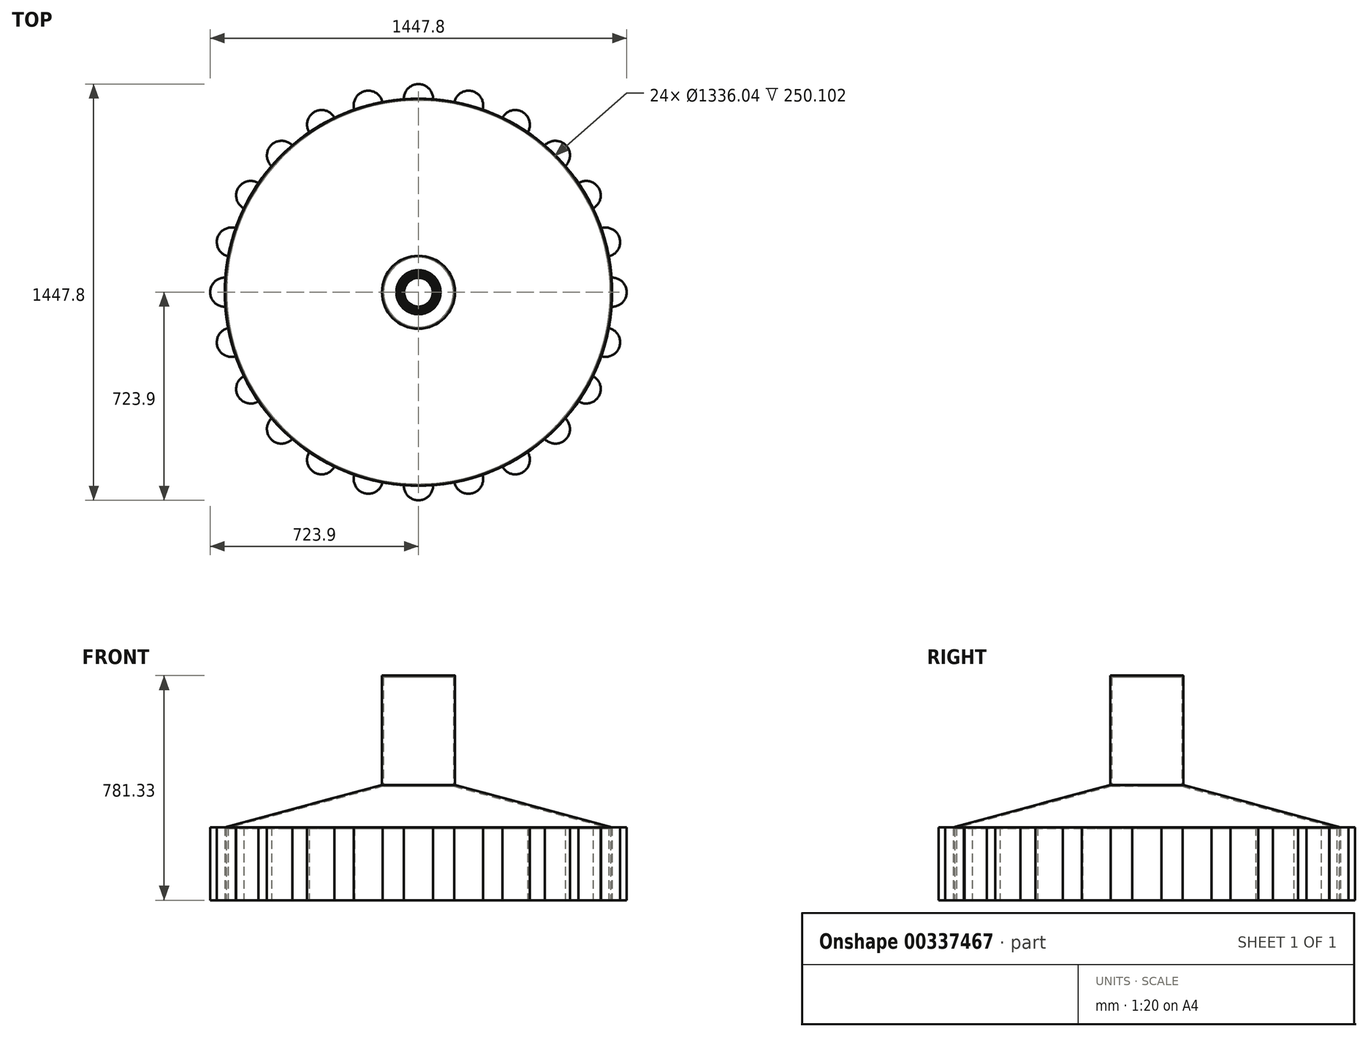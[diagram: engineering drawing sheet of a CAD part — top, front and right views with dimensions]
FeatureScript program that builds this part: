
annotation { "Feature Type Name" : "Feature", "Feature Type Description" : "" }
export const myFeature = defineFeature(function(context is Context, id is Id, definition is map)
    precondition{}
    {
        {
            var Q0;
            Q0=qCreatedBy(makeId("Front.planeOp"),FACE);
            var sketch = newSketch(context, id + "F0", { "sketchPlane" : qUnion([Q0])});
            skLineSegment(sketch, "E0", {"start": v(-673.1, 0) * mm, "end": v(-673.1, 254) * mm});
            skLineSegment(sketch, "E1", {"start": v(-673.1, 254) * mm, "end": v(-127, 400.33) * mm});
            skLineSegment(sketch, "E2", {"start": v(-127, 400.33) * mm, "end": v(-127, 781.33) * mm});
            skLineSegment(sketch, "E3", {"start": v(0, 0) * mm, "end": v(0, 880.24) * mm, "construction": true});
            skLineSegment(sketch, "E4", {"start": v(-127, 781.33) * mm, "end": v(0, 781.33) * mm});
            skLineSegment(sketch, "E5", {"start": v(0, 781.33) * mm, "end": v(0, 0) * mm});
            skLineSegment(sketch, "E6", {"start": v(-673.1, 0) * mm, "end": v(0, 0) * mm});
            skSolve(sketch);
        }
        {
            var Q0;
            Q0=makeQuery(id+"F0.imprint","IMPRINT",FACE,{"disambiguationData":[TD([[makeQuery(id+"F0.imprint","IMPRINT",EDGE,{"derivedFrom":sQuery(id+"F0.wireOp",EDGE,"E0")}),-1.0]])]});
            var Q1;
            Q1=sQuery(id+"F0.wireOp",EDGE,"E3");
            revolve(context, id + "F1", {"entities" : qUnion([Q0]), "axis" : qUnion([Q1]), "revolveType" : RevolveType.FULL});
        }
        {
            var Q0;
            Q0=makeQuery(id+"F1.opRevolve","SWEPT_FACE",FACE,{"disambiguationData":[OSD([sQuery(id+"F0.wireOp",EDGE,"E6")])]});
            shell(context, id + "F2", {"entities" : qUnion([Q0]), "thickness" : 5.08 * mm});
        }
        {
            var Q0;
            Q0=makeQuery(id+"F1.opRevolve","SWEPT_FACE",FACE,{"disambiguationData":[OSD([sQuery(id+"F0.wireOp",EDGE,"E4")])]});
            var sketch = newSketch(context, id + "F3", { "sketchPlane" : qUnion([Q0])});
            skCircle(sketch, "E7", {"center": v(0, -13.41) * mm, "radius": 63.5 * mm});
            skSolve(sketch);
        }
        {
            var Q0;
            Q0=makeQuery(id+"F3.imprint","IMPRINT",FACE,{"disambiguationData":[TD([[makeQuery(id+"F3.imprint","IMPRINT",EDGE,{"derivedFrom":sQuery(id+"F3.wireOp",EDGE,"E7")}),1.0]])]});
            extrude(context, id + "F4", {"entities" : qUnion([Q0]), "operationType" : NewBodyOperationType.REMOVE, "endBound" : BoundingType.THROUGH_ALL, "oppositeDirection" : true, "depth" : 25.4 * mm});
        }
        {
            var Q0;
            Q0=makeQuery(id+"F1.opRevolve","SWEPT_FACE",FACE,{"disambiguationData":[OSD([sQuery(id+"F0.wireOp",EDGE,"E6")])]});
            var sketch = newSketch(context, id + "F5", { "sketchPlane" : qUnion([Q0])});
            skLineSegment(sketch, "E8", {"start": v(13.8, 0) * mm, "end": v(871.86, 0) * mm, "construction": true});
            skArc(sketch, "E9", {"start": v(671.18, -50.76) * mm, "mid": v(723.9, 0) * mm, "end": v(671.18, 50.76) * mm});
            skArc(sketch, "E10", {"start": v(671.18, -50.76) * mm, "mid": v(673.1, 0) * mm, "end": v(671.18, 50.76) * mm});
            skSolve(sketch);
        }
        {
            var Q0;
            Q0=makeQuery(id+"F5.imprint","IMPRINT",FACE,{"disambiguationData":[TD([[makeQuery(id+"F5.imprint","IMPRINT",EDGE,{"derivedFrom":sQuery(id+"F5.wireOp",EDGE,"E9")}),1.0]])]});
            extrude(context, id + "F6", {"entities" : qUnion([Q0]), "operationType" : NewBodyOperationType.ADD, "oppositeDirection" : true, "depth" : 254 * mm});
        }
        {
            var Q0;
            Q0=makeQuery(id+"F1.opRevolve","SWEPT_BODY",BODY,{"disambiguationData":[OSD([sQuery(id+"F0.wireOp",EDGE,"E0"),sQuery(id+"F0.wireOp",EDGE,"E1"),sQuery(id+"F0.wireOp",EDGE,"E2"),sQuery(id+"F0.wireOp",EDGE,"E4"),sQuery(id+"F0.wireOp",EDGE,"E5"),sQuery(id+"F0.wireOp",EDGE,"E6")])]});
            var Q1;
            Q1=makeQuery(id+"F1.opRevolve","SWEPT_EDGE",EDGE,{"disambiguationData":[OSD([sQuery(id+"F0.wireOp",EDGE,"E2"),sQuery(id+"F0.wireOp",EDGE,"E4")])]});
            circularPattern(context, id + "F7", {"entities" : qUnion([Q0]), "axis" : qUnion([Q1]), "angle" : 360 * degree, "instanceCount" : 24, "equalSpace" : true});
        }
    });
